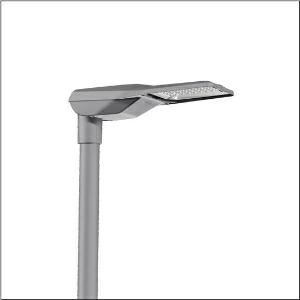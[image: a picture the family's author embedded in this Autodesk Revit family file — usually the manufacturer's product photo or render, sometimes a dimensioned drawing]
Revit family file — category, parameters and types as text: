
# Revit family: streetlight_sl_21_mini___st1_5a_5xe6p33a08gb_8a0c
name_source: partatom
category: Lighting Fixtures
units: mm (PartAtom-declared; Revit-internal decimal feet)

## family parameters
Cut with Voids When Loaded = No
Host = Face
Light Source = No
Part Type = Normal
Room Calculation Point = No
Round Connector Dimension = Use Diameter
Shared = No

## types (1)
- --- (1 x LED, 5840 lm, 40.4 W, 3000K)
    Apparent Load = 40 VA
    CIE Flux Codes = 22 53 95 100 100
    Color Rendering = 70
    Color Temperature = 3000K
    Default Elevation = 1800 mm
    Description = Streetlight SL 21 mini, mast luminaire, primary light control with lens, of PMMA, primary optical cover: cover, of toughened safety glass, transparent, light distribution: ST1.5a, light emission: direct distribution, primary light characteristic: asymmetric, installation type: post-top, side-entry, LED, 3G 1.5mm², High Power LED, rated luminous flux: 5.840lm, luminous efficacy: 145lm/W, light colour: 730, colour temperature: 3000K, control: overheat protection, constant luminous flux control, time-dependent luminous flux control, flexible luminous flux parameterisation, mains connection: 230..240V, AC, 50/60Hz, connection cable pre-assembled, cable length: 6,5m, wiring characteristics: H07RN-F, start of lifetime: 40W, end of service life: 41W, reduction: 19W, luminaire housing, of diecast aluminium, powder-coated, Siteco® metallic grey (DB 702S), corrosivity category C5 mid according to DIN EN ISO 12944, please order mast flange separately, inclination adjustable: 0°, 5°, 10°, 15°, sealing non-destructively replaceable, multi-level sealing system, length: 628mm, width: 235mm, height: 110mm, mast flange for spigot size: 42mm (side-entry): 5XC10008XM4, 60/48mm (side-entry/post-top): 5XC10108XM2, 76/60mm (side-entry/post-top): 5XC10108XM1, protection rating (complete): IP66, insulation class (complete): insulation class II (safety insulation), certification: CE, ENEC, ENEC+, VDE, impact resistance: IK09, permissible operating ambient temperature for outdoor applications: -40..+50°C, standard-compliant lighting for roads and squares, packaging unit: 1 piece

Light Distribution: ST1.5a
    Height = 110 mm
    Lamp = 1 x LED
    Lamp Light Flux = 5840 lm
    Lamp Power = 40.4 W
    Lamp count = 1
    Length = 625 mm
    Luminous efficacy = 145 lm/W
    Manufacturer = Siteco
    ModVariant = No
    Model = 5XE6P33A08GB
    Number of Poles = 1
    OnlyDefault = Yes
    Power Factor = 1
    Product Name = Streetlight SL 21 mini | ST1.5a
    Product group = mast luminaire | pylon top
    ProductGroupID = 6100
    Protection Class = Protection class II
    Protection Degree = IP 66
    RLX_Detail_Level = 1
    RLX_Emergency_Light_Flux = 0 lm
    RLX_Emergency_Type = 0
    RLX_Emergency_Type_DB = No
    RlxData = <blob elided: 95557 chars, md5=4250bfea>
    Socket = socket
    Standby Power = 0 W
    System Light Flux = 5840 lm
    System Power = 40 W
    Type Comments = factory setting: luminous flux: 100 % | Output Level: 100 % | 812 mA
    Type Image = l_1003519.jpg
    URL = http://relux.com
    VarID = @adj_108641
    Voltage = 0 V
    Weight = 0.00 kg
    Width = 234 mm

## geometry (parser evidence)
native form markers: Blend x4, Sweep x11
no freeform markers — native parametric forms only
